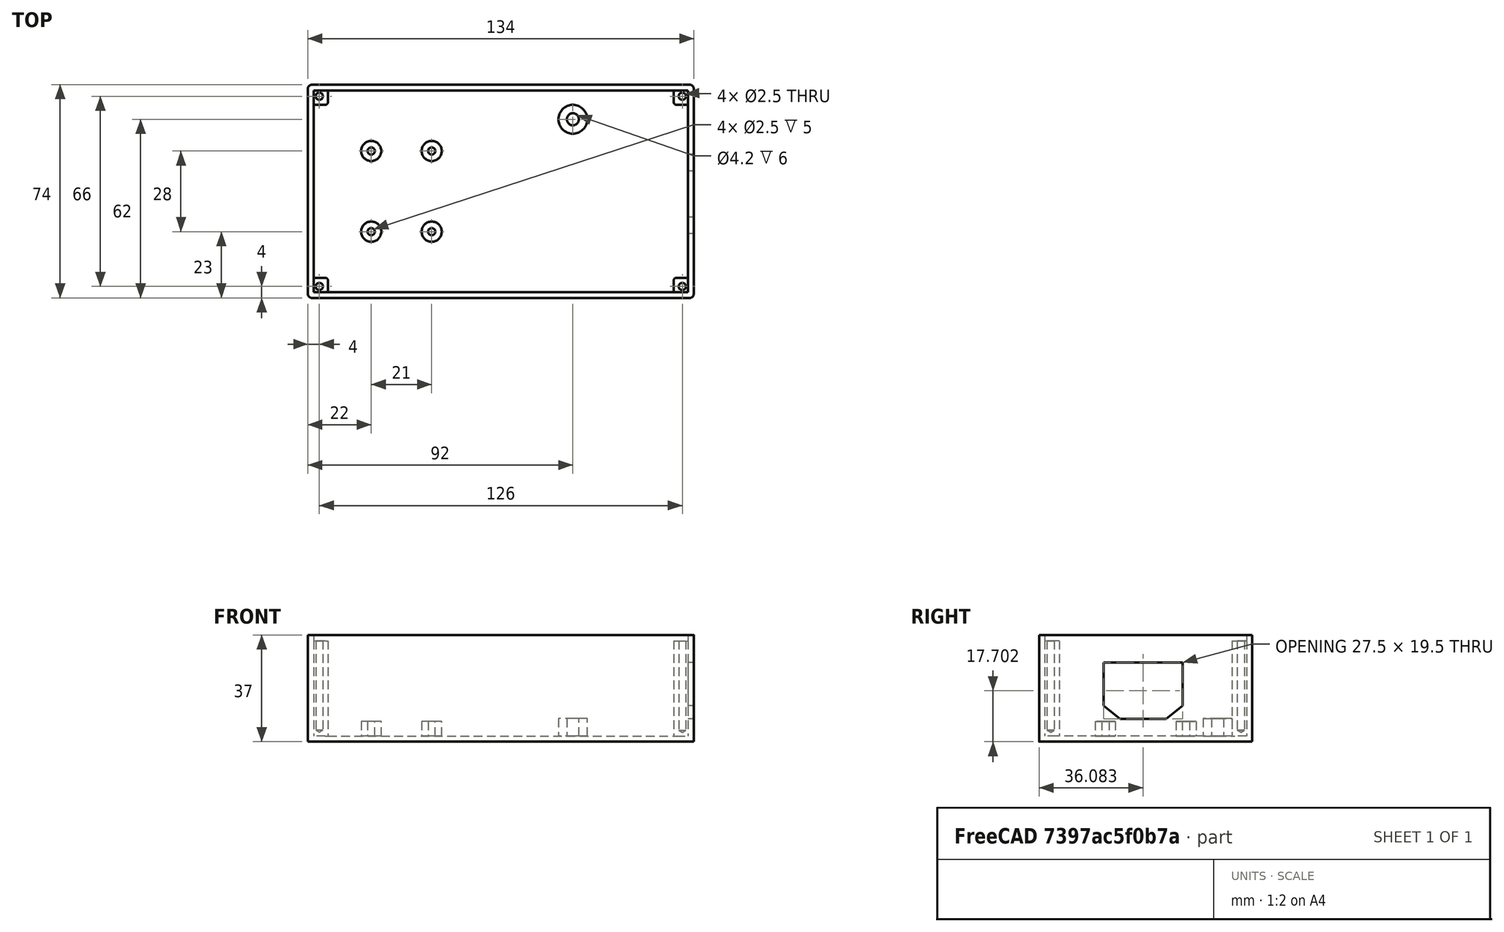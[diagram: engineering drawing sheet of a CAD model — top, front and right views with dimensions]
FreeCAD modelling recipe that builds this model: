
FCSTD DOCUMENT  (FreeCAD 0.19R24291 (Git))
Label: powerbox_bottom
License: All rights reserved
LicenseURL: http://en.wikipedia.org/wiki/All_rights_reserved
objects: Sketcher::SketchObject×7, PartDesign::Pad×3, PartDesign::Pocket×3, PartDesign::Mirrored×3, PartDesign::Plane×2, PartDesign::MultiTransform×2, Spreadsheet::Sheet×1, PartDesign::Hole×1, PartDesign::Fillet×1, PartDesign::LinearPattern×1, App::MeasureDistance×1, PartDesign::Body×1, Mesh::Feature×1
note: 32 computed .brp shape members not serialized (recipe doc carries the construction recipe); baked Part::Feature solids carry a one-line shape summary decoded from their .brp

FEATURE [Sketcher::SketchObject] Sketch
  FullyConstrained = true
  MapMode = 5
  Support = -> [XY_Plane]
  expr: Constraints[8] = <<PowerBottomDims>>.length + 2 * <<PowerBottomDims>>.thickness
  expr: Constraints[9] = <<PowerBottomDims>>.width + 2 * <<PowerBottomDims>>.thickness
  expr: Constraints[10] = (<<PowerBottomDims>>.width + 2 * <<PowerBottomDims>>.thickness) / 2
  expr: Constraints[11] = (<<PowerBottomDims>>.length + 2 * <<PowerBottomDims>>.thickness) / 2
  sketch-geometry (4):
    g0: LineSegment StartX=-67 StartY=37 StartZ=0 EndX=67 EndY=37 EndZ=0
    g1: LineSegment StartX=67 StartY=37 StartZ=0 EndX=67 EndY=-37 EndZ=0
    g2: LineSegment StartX=67 StartY=-37 StartZ=0 EndX=-67 EndY=-37 EndZ=0
    g3: LineSegment StartX=-67 StartY=-37 StartZ=0 EndX=-67 EndY=37 EndZ=0
  constraints (12):
    c: Coincident(g0,g1)
    c: Coincident(g1,g2)
    c: Coincident(g2,g3)
    c: Coincident(g3,g0)
    c: Horizontal(g0)
    c: Horizontal(g2)
    c: Vertical(g1)
    c: Vertical(g3)
    c: DistanceX(g0,g0) = 134
    c: DistanceY(g1,g1) = 74
    c: Distance(g-1,g0) = 37
    c: Distance(g-1,g1) = 67
FEATURE [Spreadsheet::Sheet] Spreadsheet  label="PowerBottomDims"
  cells = A1=Width; B1(width)==70mm; A2=Length; B2(length)==130mm; A3=Height; B3(height)==35mm; A4=Thickness; B4(thickness)==2mm
FEATURE [PartDesign::Pad] Pad
  Direction = (1,1,1)
  Length = 37
  Length2 = 100
  Profile = -> Sketch
  Type = 0
  expr: Length = <<PowerBottomDims>>.height + <<PowerBottomDims>>.thickness
FEATURE [PartDesign::Plane] DatumPlane
  Length = 153.916
  MapMode = 5
  Placement = pos=(0,0,37) rot=(0,0,1;0rad)
  ResizeMode = 0
  Support = -> [Pad]
  Width = 93.9158
FEATURE [Sketcher::SketchObject] Sketch001
  FullyConstrained = true
  MapMode = 5
  Placement = pos=(0,0,37) rot=(0,0,1;0rad)
  Support = -> [DatumPlane]
  expr: Constraints[27] = <<PowerBottomDims>>.length / 2
  expr: Constraints[5] = <<PowerBottomDims>>.length / 2
  expr: Constraints[4] = <<PowerBottomDims>>.width / 2
  expr: Constraints[28] = <<PowerBottomDims>>.width / 2
  sketch-geometry (16):
    g0: LineSegment StartX=-60 StartY=35 StartZ=0 EndX=60 EndY=35 EndZ=0
    g1: LineSegment StartX=65 StartY=30 StartZ=0 EndX=65 EndY=-30 EndZ=0
    g2: LineSegment StartX=60 StartY=-35 StartZ=0 EndX=-60 EndY=-35 EndZ=0
    g3: LineSegment StartX=-65 StartY=-30 StartZ=0 EndX=-65 EndY=30 EndZ=0
    g4: LineSegment StartX=-60 StartY=35 StartZ=0 EndX=-60 EndY=31 EndZ=0
    g5: LineSegment StartX=-61 StartY=30 StartZ=0 EndX=-65 EndY=30 EndZ=0
    g6: ArcOfCircle CenterX=-61 CenterY=31 CenterZ=0 NormalX=0 NormalY=0 NormalZ=1 AngleXU=0 Radius=1 StartAngle=4.71239 EndAngle=6.28319
    g7: LineSegment StartX=60 StartY=35 StartZ=0 EndX=60 EndY=31 EndZ=0
    g8: LineSegment StartX=61 StartY=30 StartZ=0 EndX=65 EndY=30 EndZ=0
    g9: ArcOfCircle CenterX=61 CenterY=31 CenterZ=0 NormalX=0 NormalY=0 NormalZ=1 AngleXU=0 Radius=1 StartAngle=3.14159 EndAngle=4.71239
    g10: LineSegment StartX=65 StartY=-30 StartZ=0 EndX=61 EndY=-30 EndZ=0
    g11: LineSegment StartX=60 StartY=-31 StartZ=0 EndX=60 EndY=-35 EndZ=0
    g12: LineSegment StartX=-65 StartY=-30 StartZ=0 EndX=-61 EndY=-30 EndZ=0
    g13: LineSegment StartX=-60 StartY=-31 StartZ=0 EndX=-60 EndY=-35 EndZ=0
    g14: ArcOfCircle CenterX=61 CenterY=-31 CenterZ=0 NormalX=0 NormalY=0 NormalZ=1 AngleXU=0 Radius=1 StartAngle=1.5708 EndAngle=3.14159
    g15: ArcOfCircle CenterX=-61 CenterY=-31 CenterZ=0 NormalX=0 NormalY=0 NormalZ=1 AngleXU=0 Radius=1 StartAngle=7e-16 EndAngle=1.5708
  constraints (44):
    c: Horizontal(g0)
    c: Horizontal(g2)
    c: Vertical(g1)
    c: Vertical(g3)
    c: Distance(g-1,g0) = 35
    c: Distance(g-1,g1) = 65
    c: Horizontal(g5)
    c: Vertical(g4)
    c: Tangent(g4,g6) = 1.5708
    c: Tangent(g5,g6) = 1.5708
    c: Radius(g6) = 1
    c: Horizontal(g8)
    c: Vertical(g7)
    c: Tangent(g7,g9) = -1.5708
    c: Tangent(g8,g9) = -1.5708
    c: Coincident(g4,g0)
    c: Coincident(g5,g3)
    c: Coincident(g7,g0)
    c: Coincident(g8,g1)
    c: Horizontal(g10)
    c: Vertical(g11)
    c: Coincident(g2,g11)
    c: Coincident(g10,g1)
    c: Horizontal(g12)
    c: Vertical(g13)
    c: Coincident(g12,g3)
    c: Coincident(g13,g2)
    c: Distance(g-1,g3) = 65
    c: Distance(g-1,g2) = 35
    c: DistanceY(g4,g4) = 4
    c: Equal(g4,g5)
    c: Equal(g7,g4)
    c: Equal(g7,g8)
    c: Tangent(g10,g14) = -1.5708
    c: Tangent(g11,g14) = -1.5708
    c: Tangent(g12,g15) = 1.5708
    c: Tangent(g13,g15) = 1.5708
    c: Equal(g10,g8)
    c: Equal(g10,g11)
    c: Equal(g6,g9)
    c: Equal(g9,g14)
    c: Equal(g11,g13)
    c: Equal(g12,g13)
    c: Equal(g15,g14)
FEATURE [PartDesign::Pocket] Pocket
  BaseFeature = -> Pad
  Length = 35
  Length2 = 100
  Profile = -> Sketch001
  Type = 0
  expr: Length = <<PowerBottomDims>>.height
FEATURE [Sketcher::SketchObject] Sketch002
  FullyConstrained = false
  MapMode = 5
  Placement = pos=(67,0,0) rot=(0.57735,0.57735,0.57735;2.0944rad)
  Support = -> [Pocket]
  sketch-geometry (6):
    g0: LineSegment StartX=-8.91752 StartY=7.95185 StartZ=0 EndX=7.08248 EndY=7.95185 EndZ=0
    g1: LineSegment StartX=7.08248 StartY=7.95185 StartZ=0 EndX=12.8325 EndY=12.4519 EndZ=0
    g2: LineSegment StartX=12.8325 StartY=12.4519 StartZ=0 EndX=12.8325 EndY=27.4519 EndZ=0
    g3: LineSegment StartX=12.8325 StartY=27.4519 StartZ=0 EndX=-14.6675 EndY=27.4519 EndZ=0
    g4: LineSegment StartX=-14.6675 StartY=27.4519 StartZ=0 EndX=-14.6675 EndY=12.4519 EndZ=0
    g5: LineSegment StartX=-14.6675 StartY=12.4519 StartZ=0 EndX=-8.91752 EndY=7.95185 EndZ=0
  constraints (16):
    c: Horizontal(g0)
    c: Coincident(g0,g1)
    c: Coincident(g1,g2)
    c: Vertical(g2)
    c: Coincident(g2,g3)
    c: Horizontal(g3)
    c: Coincident(g3,g4)
    c: Vertical(g4)
    c: Coincident(g4,g5)
    c: Coincident(g5,g0)
    c: Equal(g5,g1)
    c: Equal(g4,g2)
    c: DistanceX(g3,g3) = 27.5
    c: Distance(g2,g0) = 19.5
    c: DistanceX(g0,g0) = 16
    c: DistanceY(g2,g2) = 15
FEATURE [PartDesign::Pocket] Pocket001
  BaseFeature = -> Pocket
  Length = 5
  Length2 = 100
  Profile = -> Sketch002
  Type = 2
FEATURE [Sketcher::SketchObject] Sketch003
  FullyConstrained = true
  MapMode = 5
  Placement = pos=(0,0,37) rot=(0,0,1;0rad)
  Support = -> [DatumPlane]
  expr: Constraints[0] = <<PowerBottomDims>>.width / 2 - <<PowerBottomDims>>.thickness
  expr: Constraints[1] = 2.5 / 2
  expr: Constraints[2] = <<PowerBottomDims>>.length / 2 - <<PowerBottomDims>>.thickness
  sketch-geometry (1):
    g0: Circle CenterX=-63 CenterY=-33 CenterZ=0 NormalX=0 NormalY=0 NormalZ=1 AngleXU=0 Radius=1.25
  constraints (3):
    c: DistanceY(g0,g-1) = 33
    c: Radius(g0) = 1.25
    c: DistanceX(g0,g-1) = 63
FEATURE [PartDesign::Hole] Hole
  BaseFeature = -> Pocket001
  Depth = 33
  DepthType = 0
  Diameter = 2.5
  DrillForDepth = false
  DrillPoint = 1
  DrillPointAngle = 118
  HoleCutCountersinkAngle = 90
  HoleCutCustomValues = false
  HoleCutDepth = 2.25
  HoleCutDiameter = 6
  HoleCutType = 0
  ModelActualThread = false
  Profile = -> Sketch003
  Tapered = false
  TaperedAngle = 90
  ThreadAngle = 0
  ThreadClass = 0
  ThreadCutOffInner = 0
  ThreadCutOffOuter = 0
  ThreadDirection = 0
  ThreadFit = 0
  ThreadPitch = 0
  ThreadSize = 0
  ThreadType = 0
  Threaded = false
  expr: Depth = <<PowerBottomDims>>.height - <<PowerBottomDims>>.thickness
FEATURE [PartDesign::Mirrored] Mirrored
  MirrorPlane = -> Sketch003 [V_Axis]
FEATURE [PartDesign::Mirrored] Mirrored001
  MirrorPlane = -> Sketch003 [H_Axis]
FEATURE [PartDesign::MultiTransform] MultiTransform
  BaseFeature = -> Hole
  Originals = -> [Hole]
  Transformations = -> [Mirrored,Mirrored001]
FEATURE [PartDesign::Fillet] Fillet
  Base = -> MultiTransform [Edge10,Edge2,Edge5,Edge1]
  BaseFeature = -> MultiTransform
  Radius = 1.5
  SupportTransform = false
FEATURE [PartDesign::Plane] DatumPlane001
  Length = 153.916
  MapMode = 5
  Placement = pos=(0,0,2) rot=(0,0,1;0rad)
  ResizeMode = 0
  Support = -> [Fillet]
  Width = 93.9158
FEATURE [Sketcher::SketchObject] Sketch004
  FullyConstrained = true
  MapMode = 5
  Placement = pos=(0,0,2) rot=(0,0,1;0rad)
  Support = -> [Fillet]
  expr: Constraints[1] = <<PowerBottomDims>>.width / 2 - 10mm
  expr: Constraints[3] = 4.2 / 2
  expr: Constraints[4] = <<PowerBottomDims>>.length / 2 - 40mm
  sketch-geometry (2):
    g0: Circle CenterX=25 CenterY=25 CenterZ=0 NormalX=0 NormalY=0 NormalZ=1 AngleXU=0 Radius=5
    g1: Circle CenterX=25 CenterY=25 CenterZ=0 NormalX=0 NormalY=0 NormalZ=1 AngleXU=0 Radius=2.1
  constraints (5):
    c: Coincident(g1,g0)
    c: DistanceY(g-1,g0) = 25
    c: Radius(g0) = 5
    c: Radius(g1) = 2.1
    c: DistanceX(g-1,g0) = 25
FEATURE [PartDesign::Pad] Pad001
  BaseFeature = -> Fillet
  Direction = (1,1,1)
  Length = 6
  Length2 = 100
  Profile = -> Sketch004
  Type = 0
FEATURE [Sketcher::SketchObject] Sketch005
  FullyConstrained = true
  MapMode = 5
  Placement = pos=(0,0,2) rot=(0,0,1;0rad)
  Support = -> [DatumPlane001]
  expr: Constraints[1] = 2.5 / 2
  expr: Constraints[3] = <<PowerBottomDims>>.length / 2 - 20mm
  expr: Constraints[4] = 28 / 2
  sketch-geometry (2):
    g0: Circle CenterX=-45 CenterY=14 CenterZ=0 NormalX=0 NormalY=0 NormalZ=1 AngleXU=0 Radius=3.5
    g1: Circle CenterX=-45 CenterY=14 CenterZ=0 NormalX=0 NormalY=0 NormalZ=1 AngleXU=0 Radius=1.25
  constraints (5):
    c: Coincident(g1,g0)
    c: Radius(g1) = 1.25
    c: Radius(g0) = 3.5
    c: DistanceX(g0,g-1) = 45
    c: DistanceY(g-1,g0) = 14
FEATURE [PartDesign::Pad] Pad002
  BaseFeature = -> Pad001
  Direction = (1,1,1)
  Length = 5
  Length2 = 100
  Profile = -> Sketch005
  Type = 0
FEATURE [PartDesign::LinearPattern] LinearPattern
  Direction = -> Sketch005 [H_Axis]
  Length = 21
  Occurrences = 2
FEATURE [PartDesign::Mirrored] Mirrored002
  MirrorPlane = -> Sketch005 [H_Axis]
FEATURE [PartDesign::MultiTransform] MultiTransform001
  BaseFeature = -> Pad002
  Originals = -> [Pad002]
  Transformations = -> [LinearPattern,Mirrored002]
FEATURE [App::MeasureDistance] Distance  label="Distance: 43.91 mm"
  Distance = 43.9134
  P1 = (25.461,22.8891,8)
  P2 = (28.6659,-20.4942,2)
FEATURE [Sketcher::SketchObject] Sketch006
  FullyConstrained = true
  MapMode = 5
  Placement = pos=(0,0,37) rot=(0,0,1;0rad)
  Support = -> [DatumPlane]
  expr: Constraints[8] = <<PowerBottomDims>>.width / 2
  expr: Constraints[9] = <<PowerBottomDims>>.width / 2
  expr: Constraints[10] = <<PowerBottomDims>>.length / 2
  expr: Constraints[11] = <<PowerBottomDims>>.length / 2
  sketch-geometry (4):
    g0: LineSegment StartX=-65 StartY=35 StartZ=0 EndX=65 EndY=35 EndZ=0
    g1: LineSegment StartX=65 StartY=35 StartZ=0 EndX=65 EndY=-35 EndZ=0
    g2: LineSegment StartX=65 StartY=-35 StartZ=0 EndX=-65 EndY=-35 EndZ=0
    g3: LineSegment StartX=-65 StartY=-35 StartZ=0 EndX=-65 EndY=35 EndZ=0
  constraints (12):
    c: Coincident(g0,g1)
    c: Coincident(g1,g2)
    c: Coincident(g2,g3)
    c: Coincident(g3,g0)
    c: Horizontal(g0)
    c: Horizontal(g2)
    c: Vertical(g1)
    c: Vertical(g3)
    c: Distance(g-1,g0) = 35
    c: Distance(g-1,g2) = 35
    c: Distance(g-1,g1) = 65
    c: Distance(g-1,g3) = 65
FEATURE [PartDesign::Pocket] Pocket002
  BaseFeature = -> MultiTransform001
  Length = 2
  Length2 = 100
  Profile = -> Sketch006
  Type = 0
FEATURE [PartDesign::Body] Body
  Group = -> [Sketch,Pad,DatumPlane,Sketch001,Pocket,Sketch002,Pocket001,Sketch003,Hole,MultiTransform,Mirrored,Mirrored001,Fillet,DatumPlane001,Sketch004,Pad001,Sketch005,Pad002,MultiTransform001,LinearPattern,Mirrored002,Sketch006,Pocket002]
  Origin = -> Origin
  Tip = -> Pocket002
FEATURE [Mesh::Feature] Mesh  label="Body (Meshed)"
